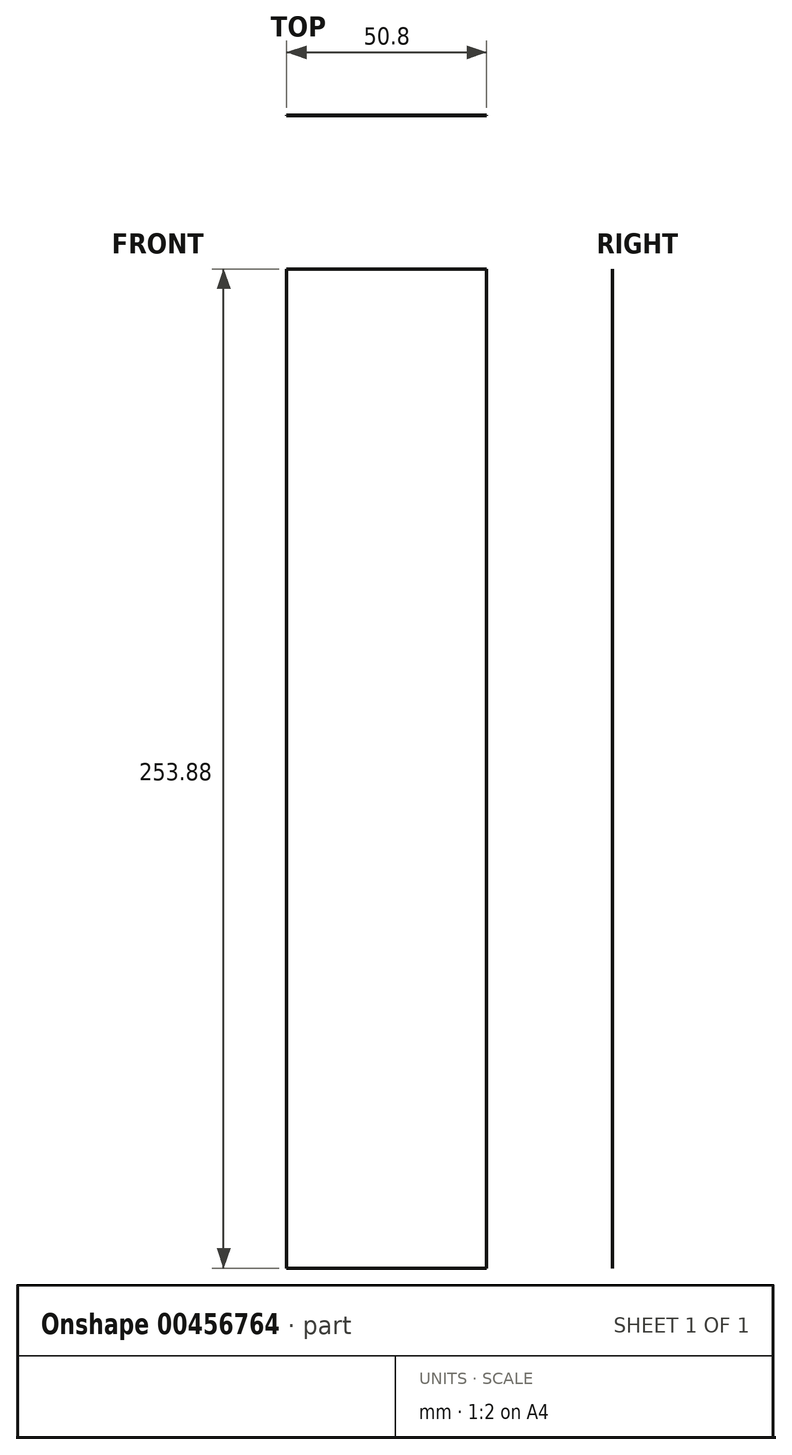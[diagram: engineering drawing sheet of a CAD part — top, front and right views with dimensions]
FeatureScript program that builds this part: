
annotation { "Feature Type Name" : "Feature", "Feature Type Description" : "" }
export const myFeature = defineFeature(function(context is Context, id is Id, definition is map)
    precondition{}
    {
        {
            var Q0;
            Q0=qCreatedBy(makeId("Front.planeOp"),FACE);
            var sketch = newSketch(context, id + "F0", { "sketchPlane" : qUnion([Q0])});
            skLineSegment(sketch, "E0.bottom", {"start": v(-25.4, 126.94) * mm, "end": v(25.4, 126.94) * mm});
            skLineSegment(sketch, "E0.top", {"start": v(-25.4, -126.94) * mm, "end": v(25.4, -126.94) * mm});
            skLineSegment(sketch, "E0.left", {"start": v(-25.4, 126.94) * mm, "end": v(-25.4, -126.94) * mm});
            skLineSegment(sketch, "E0.right", {"start": v(25.4, 126.94) * mm, "end": v(25.4, -126.94) * mm});
            skPoint(sketch, "E0.middle", {"position": v(0, 0) * mm});
            skSolve(sketch);
        }
        {
            var Q0;
            Q0=makeQuery(id+"F0.imprint","IMPRINT",FACE,{"disambiguationData":[TD([[makeQuery(id+"F0.imprint","IMPRINT",EDGE,{"derivedFrom":sQuery(id+"F0.wireOp",EDGE,"E0.bottom")}),-1.0]])]});
            extrude(context, id + "F1", {"entities" : qUnion([Q0]), "depth" : 1 / 203.2 * mm});
        }
    });
